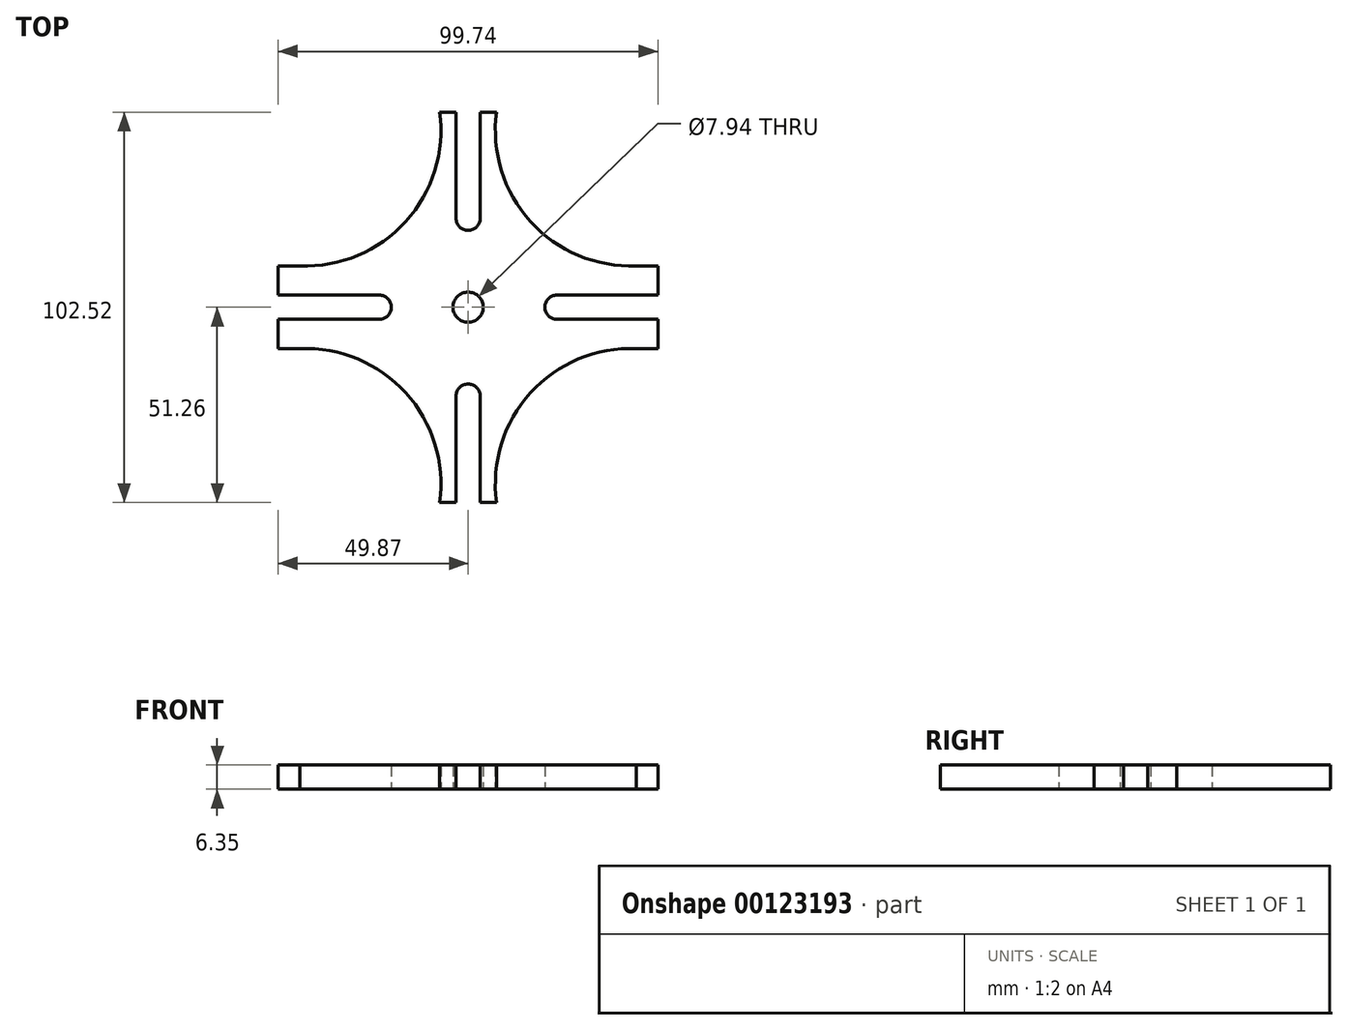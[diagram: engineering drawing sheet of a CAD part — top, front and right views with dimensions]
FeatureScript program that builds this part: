
annotation { "Feature Type Name" : "Feature", "Feature Type Description" : "" }
export const myFeature = defineFeature(function(context is Context, id is Id, definition is map)
    precondition{}
    {
        {
            var Q0;
            Q0=qCreatedBy(makeId("Top.planeOp"),FACE);
            var sketch = newSketch(context, id + "F0", { "sketchPlane" : qUnion([Q0])});
            skArc(sketch, "E0", {"start": v(-44.15, 10.88) * mm, "mid": v(-16.39, 22.5) * mm, "end": v(-7.48, 51.26) * mm});
            skLineSegment(sketch, "E1", {"start": v(0, 80.23) * mm, "end": v(0, -90.35) * mm, "construction": true});
            skLineSegment(sketch, "E2", {"start": v(-85.05, 0) * mm, "end": v(85.86, 0) * mm, "construction": true});
            skArc(sketch, "E3.MirrorCS", {"start": v(44.15, 10.88) * mm, "mid": v(16.39, 22.5) * mm, "end": v(7.48, 51.26) * mm});
            skLineSegment(sketch, "E4.MirrorCS", {"start": v(85.05, 0) * mm, "end": v(-85.86, 0) * mm, "construction": true});
            skArc(sketch, "E5.MirrorCS", {"start": v(-44.15, -10.88) * mm, "mid": v(-16.39, -22.5) * mm, "end": v(-7.48, -51.26) * mm});
            skArc(sketch, "E6.MirrorCS", {"start": v(44.15, -10.88) * mm, "mid": v(16.39, -22.5) * mm, "end": v(7.48, -51.26) * mm});
            skLineSegment(sketch, "E7", {"start": v(49.87, 3.18) * mm, "end": v(23.34, 3.18) * mm});
            skLineSegment(sketch, "E8.MirrorCS", {"start": v(49.87, -3.17) * mm, "end": v(23.34, -3.17) * mm});
            skArc(sketch, "E9", {"start": v(23.34, 3.18) * mm, "mid": v(20.16, 0) * mm, "end": v(23.34, -3.18) * mm});
            skArc(sketch, "E10.MirrorCS", {"start": v(-23.34, 3.18) * mm, "mid": v(-20.16, 0) * mm, "end": v(-23.34, -3.18) * mm});
            skLineSegment(sketch, "E11.MirrorCS", {"start": v(-49.87, 3.18) * mm, "end": v(-23.34, 3.18) * mm});
            skLineSegment(sketch, "E12.MirrorCS", {"start": v(-49.87, -3.17) * mm, "end": v(-23.34, -3.17) * mm});
            skLineSegment(sketch, "E13", {"start": v(3.18, 51.26) * mm, "end": v(3.18, 23.34) * mm});
            skLineSegment(sketch, "E14.MirrorCS", {"start": v(-3.18, 51.26) * mm, "end": v(-3.18, 23.34) * mm});
            skArc(sketch, "E15", {"start": v(-3.18, 23.34) * mm, "mid": v(0, 20.17) * mm, "end": v(3.18, 23.34) * mm});
            skArc(sketch, "E16.MirrorCS", {"start": v(-3.18, -23.34) * mm, "mid": v(0, -20.17) * mm, "end": v(3.18, -23.34) * mm});
            skLineSegment(sketch, "E17.MirrorCS", {"start": v(3.18, -51.26) * mm, "end": v(3.18, -23.34) * mm});
            skLineSegment(sketch, "E18.MirrorCS", {"start": v(-3.18, -51.26) * mm, "end": v(-3.18, -23.34) * mm});
            skLineSegment(sketch, "E19", {"start": v(-49.87, 10.88) * mm, "end": v(-49.87, 3.17) * mm});
            skLineSegment(sketch, "E20", {"start": v(-7.48, -51.26) * mm, "end": v(-3.17, -51.26) * mm});
            skLineSegment(sketch, "E21", {"start": v(49.87, -10.88) * mm, "end": v(49.87, -3.17) * mm});
            skLineSegment(sketch, "E22", {"start": v(7.48, 51.26) * mm, "end": v(3.18, 51.26) * mm});
            skPoint(sketch, "E23", {"position": v(-49.87, 3.17) * mm});
            skPoint(sketch, "E24", {"position": v(-49.87, -3.18) * mm});
            skPoint(sketch, "E25", {"position": v(-3.17, -51.26) * mm});
            skPoint(sketch, "E26", {"position": v(3.18, -51.26) * mm});
            skPoint(sketch, "E27.MirrorP", {"position": v(-3.17, 51.26) * mm});
            skPoint(sketch, "E28.MirrorP", {"position": v(3.18, 51.26) * mm});
            skLineSegment(sketch, "E29.MirrorCS", {"start": v(0, -80.23) * mm, "end": v(0, 90.35) * mm, "construction": true});
            skPoint(sketch, "E30.MirrorP", {"position": v(49.87, 3.18) * mm});
            skPoint(sketch, "E31.MirrorP", {"position": v(49.87, -3.17) * mm});
            skLineSegment(sketch, "E32.trimOffspring", {"start": v(-3.17, 51.26) * mm, "end": v(-7.48, 51.26) * mm});
            skLineSegment(sketch, "E33.trimOffspring", {"start": v(-49.87, -3.18) * mm, "end": v(-49.87, -10.88) * mm});
            skLineSegment(sketch, "E34.trimOffspring", {"start": v(3.18, -51.26) * mm, "end": v(7.48, -51.26) * mm});
            skLineSegment(sketch, "E35.trimOffspring", {"start": v(49.87, 3.18) * mm, "end": v(49.87, 10.88) * mm});
            skPoint(sketch, "E36", {"position": v(-44.15, -10.88) * mm});
            skPoint(sketch, "E37", {"position": v(-49.87, -10.88) * mm});
            skLineSegment(sketch, "E38", {"start": v(-49.87, -10.88) * mm, "end": v(-44.15, -10.88) * mm});
            skLineSegment(sketch, "E39.MirrorCS", {"start": v(-49.87, 10.88) * mm, "end": v(-44.15, 10.88) * mm});
            skLineSegment(sketch, "E40.MirrorCS", {"start": v(-49.87, 3.17) * mm, "end": v(-49.87, 10.88) * mm});
            skLineSegment(sketch, "E41.MirrorCS", {"start": v(49.87, -10.88) * mm, "end": v(44.15, -10.88) * mm});
            skLineSegment(sketch, "E42.MirrorCS", {"start": v(49.87, -3.17) * mm, "end": v(49.87, -10.88) * mm});
            skLineSegment(sketch, "E43.MirrorCS", {"start": v(49.87, 10.88) * mm, "end": v(44.15, 10.88) * mm});
            skPoint(sketch, "E44.orphan", {"position": v(49.87, 11.57) * mm});
            skPoint(sketch, "E45.orphan", {"position": v(49.87, -11.57) * mm});
            skPoint(sketch, "E46.orphan", {"position": v(-49.87, 11.57) * mm});
            skPoint(sketch, "E47", {"position": v(7.43, -41.98) * mm});
            skPoint(sketch, "E48.MirrorP", {"position": v(7.43, 41.98) * mm});
            skPoint(sketch, "E49.MirrorP", {"position": v(-7.43, -41.98) * mm});
            skPoint(sketch, "E50.MirrorP", {"position": v(-7.43, 41.98) * mm});
            skSolve(sketch);
        }
        {
            var Q0;
            Q0 = qSketchRegion(id + "F0", true);
            extrude(context, id + "F1", {"entities" : qUnion([Q0]), "depth" : 6.35 * mm});
        }
        {
            var Q0;
            Q0=makeQuery(id+"F1.opExtrude","CAP_FACE",FACE,{"disambiguationData":[OSD([sQuery(id+"F0.wireOp",EDGE,"E0"),sQuery(id+"F0.wireOp",EDGE,"E3.MirrorCS"),sQuery(id+"F0.wireOp",EDGE,"E5.MirrorCS"),sQuery(id+"F0.wireOp",EDGE,"E6.MirrorCS"),sQuery(id+"F0.wireOp",EDGE,"E7"),sQuery(id+"F0.wireOp",EDGE,"E8.MirrorCS"),sQuery(id+"F0.wireOp",EDGE,"E9"),sQuery(id+"F0.wireOp",EDGE,"E10.MirrorCS"),sQuery(id+"F0.wireOp",EDGE,"E11.MirrorCS"),sQuery(id+"F0.wireOp",EDGE,"E12.MirrorCS"),sQuery(id+"F0.wireOp",EDGE,"E13"),sQuery(id+"F0.wireOp",EDGE,"E14.MirrorCS"),sQuery(id+"F0.wireOp",EDGE,"E15"),sQuery(id+"F0.wireOp",EDGE,"E16.MirrorCS"),sQuery(id+"F0.wireOp",EDGE,"E17.MirrorCS"),sQuery(id+"F0.wireOp",EDGE,"E18.MirrorCS"),sQuery(id+"F0.wireOp",EDGE,"E19"),sQuery(id+"F0.wireOp",EDGE,"E20"),sQuery(id+"F0.wireOp",EDGE,"E21"),sQuery(id+"F0.wireOp",EDGE,"E22"),sQuery(id+"F0.wireOp",EDGE,"E32.trimOffspring"),sQuery(id+"F0.wireOp",EDGE,"E33.trimOffspring"),sQuery(id+"F0.wireOp",EDGE,"E34.trimOffspring"),sQuery(id+"F0.wireOp",EDGE,"E35.trimOffspring")])],"isStart":true});
            var sketch = newSketch(context, id + "F2", { "sketchPlane" : qUnion([Q0])});
            skCircle(sketch, "E51", {"center": v(0, 0) * mm, "radius": 3.97 * mm});
            skSolve(sketch);
        }
        {
            var Q0;
            Q0=makeQuery(id+"F2.imprint","IMPRINT",FACE,{"disambiguationData":[TD([[makeQuery(id+"F2.imprint","IMPRINT",EDGE,{"derivedFrom":sQuery(id+"F2.wireOp",EDGE,"E51")}),1.0]])]});
            var Q1;
            Q1=sQuery(id+"F2.wireOp",EDGE,"E51");
            extrude(context, id + "F3", {"entities" : qUnion([Q0]), "operationType" : NewBodyOperationType.REMOVE, "surfaceEntities" : qUnion([Q1]), "oppositeDirection" : true, "depth" : 45.74 * mm});
        }
    });
